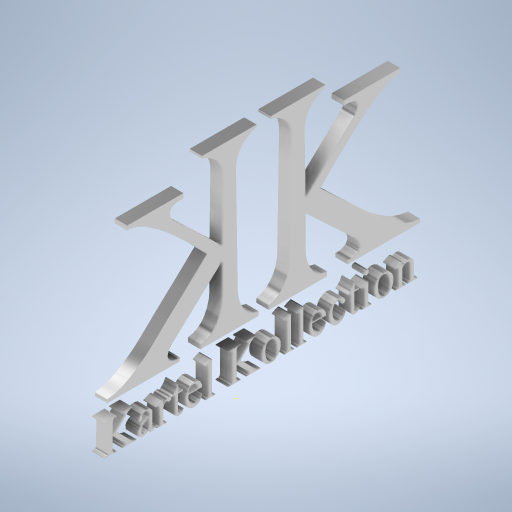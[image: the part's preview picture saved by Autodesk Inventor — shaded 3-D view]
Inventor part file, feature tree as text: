
AUTODESK INVENTOR PART (.ipt)
format: ipt  version: 2024 (Build 280153000, 153)  size: 1,355,264 bytes
history: native  units: in
note: dims shown in document units (in); Inventor stores cm internally (conversion verified against a paired STEP export)
features: extrude x4, other x2, sketch x2
ambient origin geometry x8: Origin, YZ Plane, XZ Plane, XY Plane, X Axis, Y Axis, Z Axis, Center Point
bodies: Body1 (feature_tree)
feature tree (8):
  other  "Sólido1"
  sketch  "Boceto1"  dims[d10=0.7874in d12=2.55in d13=0.3937in d15=1.0in d18=0.7874in d20=2.95in d21=0.3937in d23=1.0in]
  sketch  "Boceto2"  dims[d26=0.7874in d28=4.0in d29=0.3937in d31=1.0in d34=0.7874in d36=5.69in d37=0.3937in d39=1.0in d42=0.7874in d44=3.64in d45=0.3937in d47=1.0in d50=0.7874in d52=4.0in d53=0.3937in d55=1.0in d58=0.4in d59=0.0in d61=0.4in d62=0.0in d64=0.4in d65=0.0in d67=0.4in d68=0.0in]
  extrude  "Extrusión1"  Depth=2.95in
  extrude  "Extrusión2"  Depth=5.69in
  extrude  "Extrusión3"  Depth=0.3937in
  extrude  "Extrusión4"  Depth=4.0in
  other  "Imagen1"
